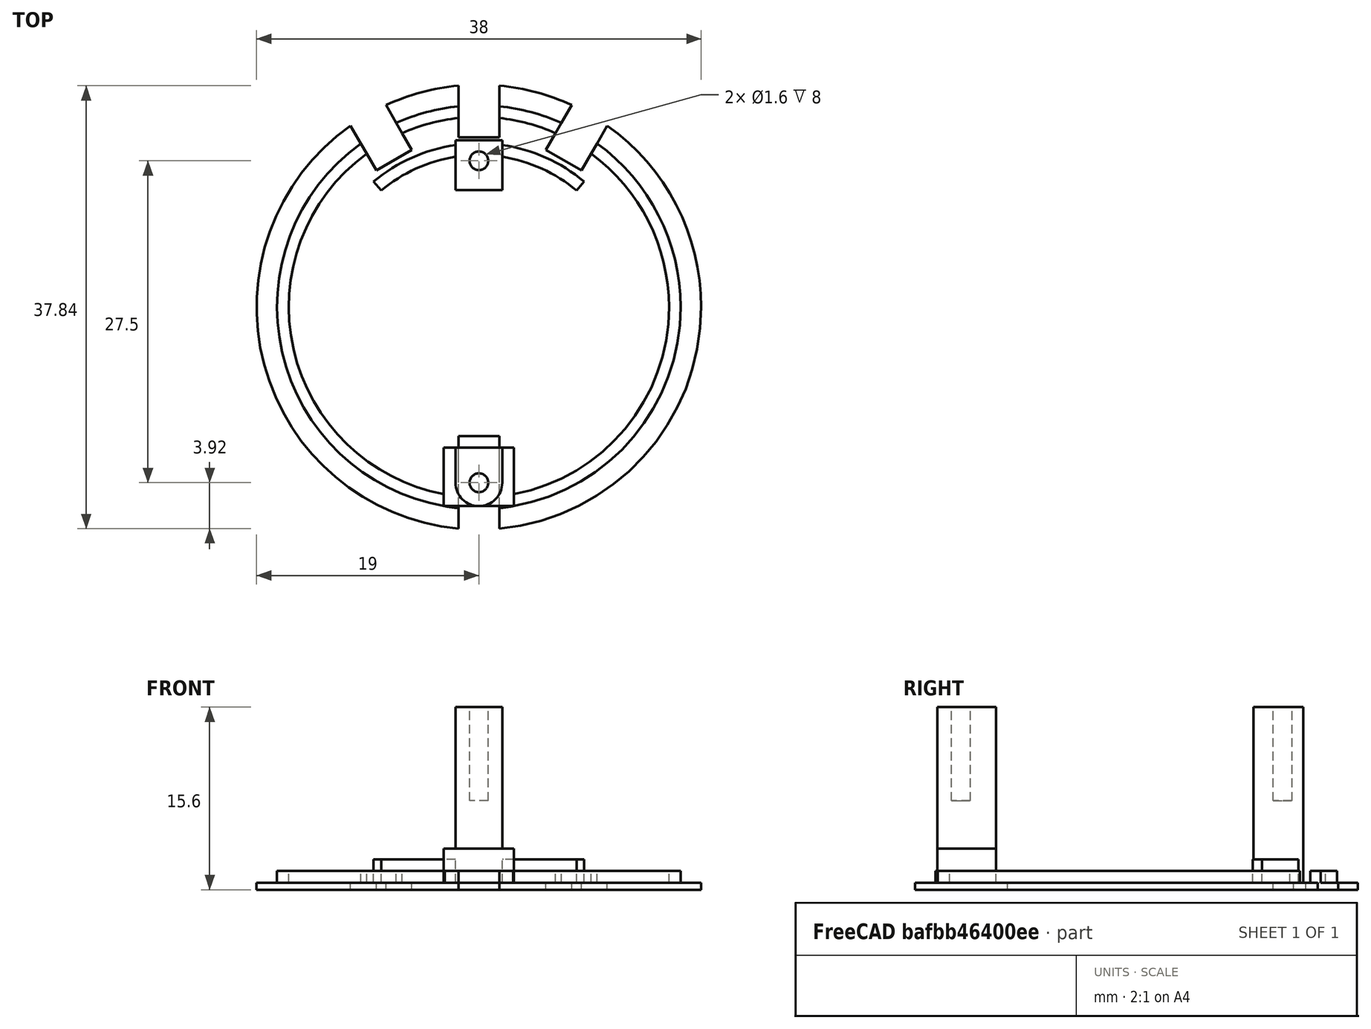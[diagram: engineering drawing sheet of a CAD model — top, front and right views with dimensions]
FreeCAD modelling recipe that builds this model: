
FCSTD DOCUMENT  (FreeCAD 0.18.4R)
Label: Servoabzweig
License: All rights reserved
LicenseURL: http://en.wikipedia.org/wiki/All_rights_reserved
objects: Part::Cylinder×8, Part::Box×7, Part::Cut×5, Part::MultiFuse×4
note: 24 computed .brp shape members not serialized (recipe doc carries the construction recipe); baked Part::Feature solids carry a one-line shape summary decoded from their .brp

FEATURE [Part::Cylinder] Cylinder  label="Base"
  Angle = 360
  AttacherType = Attacher::AttachEngine3D
  Height = 0.6
  Placement = pos=(0,0,-0.6) rot=(0,0,1;0rad)
  Radius = 19
FEATURE [Part::Cylinder] Cylinder001  label="Zylinder"
  Angle = 360
  AttacherType = Attacher::AttachEngine3D
  Height = 1
  Radius = 17.25
FEATURE [Part::Cylinder] Cylinder002  label="Zylinder001"
  Angle = 360
  AttacherType = Attacher::AttachEngine3D
  Height = 1
  Radius = 16.25
FEATURE [Part::Box] Box  label="Würfel"
  AttacherType = Attacher::AttachEngine3D
  Height = 1.6
  Length = 3.5
  Placement = pos=(-1.75,14.5,-0.6) rot=(0,0,1;0rad)
  Width = 5
FEATURE [Part::Box] Box001  label="Würfel001"
  AttacherType = Attacher::AttachEngine3D
  Height = 1.6
  Length = 3.5
  Placement = pos=(-8.76554,11.6824,-0.6) rot=(0,0,1;0.523599rad)
  Width = 5
FEATURE [Part::Box] Box002  label="Würfel002"
  AttacherType = Attacher::AttachEngine3D
  Height = 1.6
  Length = 3.5
  Placement = pos=(5.73446,13.4324,-0.6) rot=(0,0,-1;0.523599rad)
  Width = 5
FEATURE [Part::Cut] Cut
  Base = -> Cylinder001
  Tool = -> Cylinder002
FEATURE [Part::Cylinder] Cylinder003  label="Zylinder002"
  Angle = 80
  AttacherType = Attacher::AttachEngine3D
  Height = 2
  Radius = 14
FEATURE [Part::Cylinder] Cylinder004  label="Zylinder003"
  Angle = 360
  AttacherType = Attacher::AttachEngine3D
  Height = 4
  Radius = 13
FEATURE [Part::Cut] Cut002
  Base = -> Cylinder003
  Placement = pos=(0,0,0) rot=(0,0,1;0.872665rad)
  Tool = -> Cylinder004
FEATURE [Part::Cylinder] Cylinder005  label="Zylinder004"
  Angle = 360
  AttacherType = Attacher::AttachEngine3D
  Height = 14
  Placement = pos=(0,-15,1) rot=(0,0,1;0rad)
  Radius = 2
FEATURE [Part::Box] Box003  label="Würfel003"
  AttacherType = Attacher::AttachEngine3D
  Height = 14
  Length = 4
  Placement = pos=(-2,-15,1) rot=(0,0,1;0rad)
  Width = 3
FEATURE [Part::Box] Box004  label="Würfel004"
  AttacherType = Attacher::AttachEngine3D
  Height = 15
  Length = 4
  Placement = pos=(-2,10,0) rot=(0,0,1;0rad)
  Width = 4.25
FEATURE [Part::MultiFuse] Fusion002
  Shapes = -> [Cylinder005,Box003]
FEATURE [Part::Cylinder] Cylinder006  label="Zylinder005"
  Angle = 360
  AttacherType = Attacher::AttachEngine3D
  Height = 8
  Placement = pos=(0,-15,7) rot=(0,0,1;0rad)
  Radius = 0.8
FEATURE [Part::Cut] Cut003  label="Halter Hinten"
  Base = -> Fusion002
  Tool = -> Cylinder006
FEATURE [Part::Cylinder] Cylinder007  label="Zylinder006"
  Angle = 360
  AttacherType = Attacher::AttachEngine3D
  Height = 8
  Placement = pos=(0,12.5,7) rot=(0,0,1;0rad)
  Radius = 0.8
FEATURE [Part::Cut] Cut004  label="Halter Vorne"
  Base = -> Box004
  Tool = -> Cylinder007
FEATURE [Part::Box] Box005  label="Würfel005"
  AttacherType = Attacher::AttachEngine3D
  Height = 1.6
  Length = 3.5
  Placement = pos=(-1.75,-19,-0.6) rot=(0,0,1;0rad)
  Width = 8
FEATURE [Part::MultiFuse] Fusion001
  Shapes = -> [Box002,Box001,Box,Box005]
FEATURE [Part::Box] Box006  label="Würfel006"
  AttacherType = Attacher::AttachEngine3D
  Height = 3.5
  Length = 6
  Placement = pos=(-3,-17,-0.6) rot=(0,0,1;0rad)
  Width = 5
FEATURE [Part::MultiFuse] Fusion  label="Grundplatte"
  Shapes = -> [Cylinder,Cut,Box006]
FEATURE [Part::Cut] Cut001
  Base = -> Fusion
  Tool = -> Fusion001
FEATURE [Part::MultiFuse] Fusion003
  Shapes = -> [Cut002,Cut001,Cut003,Cut004]
